FCSTD DOCUMENT  (FreeCAD 1.0R39319 (Git))
Label: Week1Assignment3
License: All rights reserved
LicenseURL: https://en.wikipedia.org/wiki/All_rights_reserved
objects: Sketcher::SketchObject×1
note: 2 computed .brp shape members not serialized (recipe doc carries the construction recipe); baked Part::Feature solids carry a one-line shape summary decoded from their .brp

FEATURE [Sketcher::SketchObject] Sketch
  ArcFitTolerance = 1e-06
  FullyConstrained = true
  MakeInternals = false
  sketch-geometry (24):
    g0: ArcOfCircle CenterX=0 CenterY=139.011 CenterZ=0 NormalX=0 NormalY=0 NormalZ=1 AngleXU=0 Radius=22 StartAngle=6e-16 EndAngle=3.14159
    g1: ArcOfCircle CenterX=-1.9e-15 CenterY=111.011 CenterZ=0 NormalX=0 NormalY=0 NormalZ=1 AngleXU=0 Radius=22 StartAngle=3.14159 EndAngle=6.28319
    g2: LineSegment StartX=22 StartY=139.011 StartZ=0 EndX=22 EndY=111.011 EndZ=0
    g3: LineSegment StartX=-22 StartY=139.011 StartZ=0 EndX=-22 EndY=111.011 EndZ=0
    g4: ArcOfCircle CenterX=0 CenterY=139.011 CenterZ=0 NormalX=0 NormalY=0 NormalZ=1 AngleXU=0 Radius=10 StartAngle=1e-16 EndAngle=3.14159
    g5: LineSegment StartX=10 StartY=139.011 StartZ=0 EndX=10 EndY=125.011 EndZ=0
    g6: LineSegment StartX=-10 StartY=139.011 StartZ=0 EndX=-10 EndY=125.011 EndZ=0
    g7: ArcOfCircle CenterX=-1.9e-15 CenterY=111.011 CenterZ=0 NormalX=0 NormalY=0 NormalZ=1 AngleXU=0 Radius=12 StartAngle=3.14159 EndAngle=6.28319
    g8: LineSegment StartX=-12 StartY=111.011 StartZ=0 EndX=-12 EndY=123.596 EndZ=0
    g9: LineSegment StartX=12 StartY=111.011 StartZ=0 EndX=12 EndY=125.011 EndZ=0
    g10: ArcOfCircle CenterX=-10.5 CenterY=123.596 CenterZ=0 NormalX=0 NormalY=0 NormalZ=1 AngleXU=0 Radius=1.5 StartAngle=1.23096 EndAngle=3.14159
    g11: ArcOfCircle CenterX=10.5 CenterY=123.596 CenterZ=0 NormalX=0 NormalY=0 NormalZ=1 AngleXU=0 Radius=1.5 StartAngle=0 EndAngle=1.91063
    g12: ArcOfCircle CenterX=0 CenterY=11.0106 CenterZ=0 NormalX=0 NormalY=0 NormalZ=1 AngleXU=0 Radius=10 StartAngle=3.14159 EndAngle=6.28319
    g13: ArcOfCircle CenterX=0 CenterY=39.853 CenterZ=0 NormalX=0 NormalY=0 NormalZ=1 AngleXU=0 Radius=12 StartAngle=6.21293 EndAngle=9.49503
    g14: LineSegment StartX=11.9704 StartY=39.0106 StartZ=0 EndX=10 EndY=11.0106 EndZ=0
    g15: LineSegment StartX=-11.9704 StartY=39.0106 StartZ=0 EndX=-10 EndY=11.0106 EndZ=0
    g16: LineSegment StartX=-22 StartY=139.011 StartZ=0 EndX=-40.0386 EndY=97.6449 EndZ=0
    g17: ArcOfCircle CenterX=-10.7063 CenterY=84.8537 CenterZ=0 NormalX=0 NormalY=0 NormalZ=1 AngleXU=0 Radius=32 StartAngle=2.73038 EndAngle=3.77942
    g18: ArcOfCircle CenterX=-60.5165 CenterY=47.9357 CenterZ=0 NormalX=0 NormalY=0 NormalZ=1 AngleXU=0 Radius=30 StartAngle=5.75376 EndAngle=6.92101
    g19: ArcOfCircle CenterX=-0.0997864 CenterY=12.5829 CenterZ=0 NormalX=0 NormalY=0 NormalZ=1 AngleXU=0 Radius=40 StartAngle=2.61217 EndAngle=4.71488
    g20: LineSegment StartX=22 StartY=139.011 StartZ=0 EndX=40.0346 EndY=97.6449 EndZ=0
    g21: ArcOfCircle CenterX=10.7012 CenterY=84.8562 CenterZ=0 NormalX=0 NormalY=0 NormalZ=1 AngleXU=0 Radius=32 StartAngle=5.64239 EndAngle=6.69432
    g22: ArcOfCircle CenterX=60.4017 CenterY=47.7905 CenterZ=0 NormalX=0 NormalY=0 NormalZ=1 AngleXU=0 Radius=30 StartAngle=2.5008 EndAngle=3.66862
    g23: ArcOfCircle CenterX=-0.0997813 CenterY=12.5829 CenterZ=0 NormalX=0 NormalY=0 NormalZ=1 AngleXU=0 Radius=40 StartAngle=4.71488 EndAngle=6.81021
  constraints (57):
    c: Tangent(g0,g2) = 1.5708
    c: Tangent(g0,g3) = -1.5708
    c: Tangent(g1,g2) = 1.5708
    c: Tangent(g1,g3) = -1.5708
    c: Equal(g0,g1)
    c: Distance(g0,g1) = 28
    c: PointOnObject(g0,g-2)
    c: Block(g0)
    c: Tangent(g4,g5) = 1.5708
    c: Tangent(g4,g6) = -1.5708
    c: Tangent(g7,g8) = 1.5708
    c: Tangent(g7,g9) = -1.5708
    c: Vertical(g9)
    c: Radius(g7) = 12
    c: Coincident(g7,g1)
    c: Block(g4)
    c: DistanceY(g9,g9) = 14
    c: Equal(g6,g5)
    c: Tangent(g10,g8) = 1.5708
    c: Coincident(g10,g6)
    c: Diameter(g11) = 3
    c: Block(g11)
    c: Block(g10)
    c: Radius(g12) = 10
    c: PointOnObject(g12,g-2)
    c: DistanceY(g12,g0) = 128
    c: Tangent(g13,g14) = 1.5708
    c: Tangent(g13,g15) = -1.5708
    c: Radius(g13) = 12
    c: Coincident(g14,g12)
    c: Coincident(g15,g12)
    c: PointOnObject(g13,g-2)
    c: DistanceY(g14,g14) = 28
    c: Equal(g14,g15)
    c: Angle(g12) = 3.14159
    c: Block(g6)
    c: Block(g8)
    c: Block(g7)
    c: Coincident(g0,g16)
    c: Tangent(g16,g17) = -1.5708
    c: Tangent(g17,g18) = 1.5708
    c: Tangent(g18,g19) = 1.5708
    c: PointOnObject(g19,g-2)
    c: Radius(g17) = 32
    c: Radius(g18) = 30
    c: Radius(g19) = 40
    c: Tangent(g20,g21) = 1.5708
    c: Tangent(g21,g22) = 1.5708
    c: Tangent(g22,g23) = 1.5708
    c: Radius(g21) = 32
    c: Radius(g22) = 30
    c: Radius(g23) = 40
    c: Tangent(g23,g19)
    c: Block(g16)
    c: Block(g20)
    c: Block(g17)
    c: Block(g23)
